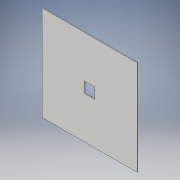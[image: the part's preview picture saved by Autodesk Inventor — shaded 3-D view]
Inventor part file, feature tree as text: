
AUTODESK INVENTOR PART (.ipt)
format: ipt  version: 2018 (Build 220112000, 112)  size: 95,232 bytes
history: native  units: in
note: dims shown in document units (in); Inventor stores cm internally (conversion verified against a paired STEP export)
features: extrude x1, sketch x1
ambient origin geometry x8: Origin, YZ Plane, XZ Plane, XY Plane, X Axis, Y Axis, Z Axis, Center Point
bodies: Solid1 (feature_tree)
feature tree (2):
  extrude  "Extrusion1"  Depth=36.0in
  sketch  "Sketch1"  dims[d0=36.0in d1=36.0in d2=4.0in d3=4.0in d4=0.25in d5=0.0in]
